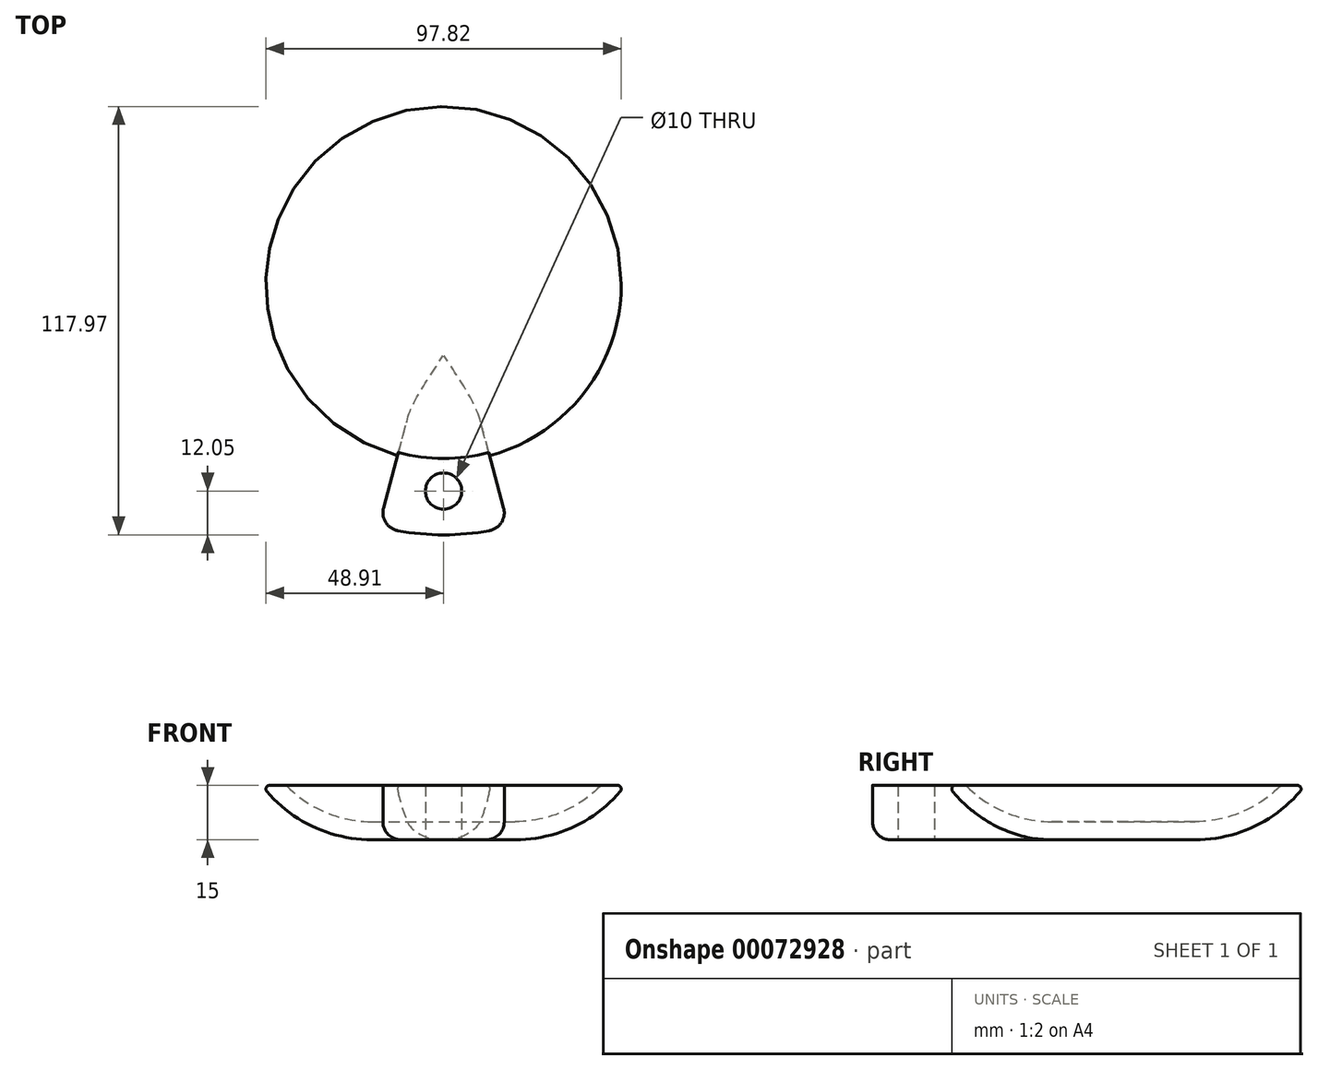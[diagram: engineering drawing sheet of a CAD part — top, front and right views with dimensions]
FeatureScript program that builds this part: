
annotation { "Feature Type Name" : "Feature", "Feature Type Description" : "" }
export const myFeature = defineFeature(function(context is Context, id is Id, definition is map)
    precondition{}
    {
        {
            var Q0;
            Q0=qCreatedBy(makeId("Top.planeOp"),FACE);
            var sketch = newSketch(context, id + "F0", { "sketchPlane" : qUnion([Q0])});
            skCircle(sketch, "E0", {"center": v(0, 0) * mm, "radius": 50 * mm});
            skSolve(sketch);
        }
        {
            var Q0;
            Q0=makeQuery(id+"F0.imprint","IMPRINT",FACE,{"disambiguationData":[TD([[makeQuery(id+"F0.imprint","IMPRINT",EDGE,{"derivedFrom":sQuery(id+"F0.wireOp",EDGE,"E0")}),1.0]])]});
            extrude(context, id + "F1", {"entities" : qUnion([Q0]), "depth" : 15 * mm});
        }
        {
            var Q0;
            Q0=makeQuery(id+"F1.opExtrude","CAP_EDGE",EDGE,{"disambiguationData":[OSD([sQuery(id+"F0.wireOp",EDGE,"E0")])],"isStart":true});
            fillet(context, id + "F2", {"entities" : qUnion([Q0]), "radius" : 38.1 * mm, "tangentPropagation" : true, "allowEdgeOverflow" : false});
        }
        {
            var Q0;
            Q0=makeQuery(id+"F1.opExtrude","CAP_FACE",FACE,{"disambiguationData":[OSD([sQuery(id+"F0.wireOp",EDGE,"E0")])],"isStart":false});
            shell(context, id + "F3", {"entities" : qUnion([Q0]), "thickness" : 5 * mm});
        }
        {
            var Q0;
            {var subQ0=sQuery(id+"F0.wireOp",EDGE,"E0");Q0=makeQuery(id+"F3.opShell","OFFSET_EDGE",EDGE,{"disambiguationData":[OSD([subQ0]),TDD([makeQuery(id+"F2.opFillet","BLEND_EDGE",EDGE,{"blendedFrom":[makeQuery(id+"F1.opExtrude","CAP_EDGE",EDGE,{"disambiguationData":[OSD([subQ0])],"isStart":true}),makeQuery(id+"F1.opExtrude","CAP_FACE",FACE,{"disambiguationData":[OSD([subQ0])],"isStart":false})],"blendedInto":[makeQuery(id+"F1.opExtrude","CAP_FACE",FACE,{"disambiguationData":[OSD([subQ0])],"isStart":false})]})])]});}
            fillet(context, id + "F4", {"entities" : qUnion([Q0]), "radius" : 1 * mm, "allowEdgeOverflow" : false});
        }
        {
            var Q0;
            {var subQ0=sQuery(id+"F0.wireOp",EDGE,"E0");Q0=makeQuery(id+"F2.opFillet","BLEND_EDGE",EDGE,{"blendedFrom":[makeQuery(id+"F1.opExtrude","CAP_EDGE",EDGE,{"disambiguationData":[OSD([subQ0])],"isStart":true}),makeQuery(id+"F1.opExtrude","CAP_FACE",FACE,{"disambiguationData":[OSD([subQ0])],"isStart":false})],"blendedInto":[makeQuery(id+"F1.opExtrude","CAP_FACE",FACE,{"disambiguationData":[OSD([subQ0])],"isStart":false})]});}
            fillet(context, id + "F5", {"entities" : qUnion([Q0]), "radius" : 1 * mm, "allowEdgeOverflow" : false});
        }
        {
            var Q0;
            Q0=qCreatedBy(makeId("Right.planeOp"),FACE);
            var sketch = newSketch(context, id + "F6", { "sketchPlane" : qUnion([Q0])});
            skLineSegment(sketch, "E1", {"start": v(-69.06, 0) * mm, "end": v(-69.06, 15) * mm});
            skLineSegment(sketch, "E2", {"start": v(-69.06, 0) * mm, "end": v(0, 0) * mm});
            skArc(sketch, "E3", {"start": v(-48.02, 15) * mm, "mid": v(-25.15, 3.84) * mm, "end": v(0, 0) * mm});
            skLineSegment(sketch, "E4", {"start": v(-48.02, 15) * mm, "end": v(-69.06, 15) * mm});
            skSolve(sketch);
        }
        {
            var Q0;
            Q0=qCreatedBy(makeId("Right.planeOp"),FACE);
            var sketch = newSketch(context, id + "F7", { "sketchPlane" : qUnion([Q0])});
            skLineSegment(sketch, "E5", {"start": v(0, 44.96) * mm, "end": v(0, 0) * mm, "construction": true});
            skSolve(sketch);
        }
        {
            var Q0;
            Q0=makeQuery(id+"F6.imprint","IMPRINT",FACE,{"disambiguationData":[TD([[makeQuery(id+"F6.imprint","IMPRINT",EDGE,{"derivedFrom":sQuery(id+"F6.wireOp",EDGE,"E1")}),-1.0]])]});
            var Q1;
            Q1=sQuery(id+"F7.wireOp",EDGE,"E5");
            revolve(context, id + "F8", {"operationType" : NewBodyOperationType.ADD, "entities" : qUnion([Q0]), "axis" : qUnion([Q1]), "revolveType" : RevolveType.SYMMETRIC, "angle" : 30 * degree});
        }
        {
            var Q0;
            Q0=makeQuery(id+"F8.opRevolve","SWEPT_EDGE",EDGE,{"disambiguationData":[OSD([sQuery(id+"F6.wireOp",EDGE,"E1"),sQuery(id+"F6.wireOp",EDGE,"E2")])]});
            var Q1;
            Q1=makeQuery(id+"F8.opRevolve","CAP_EDGE",EDGE,{"disambiguationData":[OSD([sQuery(id+"F6.wireOp",EDGE,"E2")])],"isStart":true});
            var Q2;
            Q2=makeQuery(id+"F8.opRevolve","CAP_EDGE",EDGE,{"disambiguationData":[OSD([sQuery(id+"F6.wireOp",EDGE,"E2")])],"isStart":false});
            var Q3;
            Q3=makeQuery(id+"F8.opRevolve","CAP_EDGE",EDGE,{"disambiguationData":[OSD([sQuery(id+"F6.wireOp",EDGE,"E1")])],"isStart":true});
            var Q4;
            Q4=makeQuery(id+"F8.opRevolve","CAP_EDGE",EDGE,{"disambiguationData":[OSD([sQuery(id+"F6.wireOp",EDGE,"E1")])],"isStart":false});
            fillet(context, id + "F9", {"entities" : qUnion([Q0, Q1, Q2, Q3, Q4]), "radius" : 5 * mm, "tangentPropagation" : true, "allowEdgeOverflow" : false});
        }
        {
            var Q0;
            Q0=qCreatedBy(makeId("Top.planeOp"),FACE);
            var sketch = newSketch(context, id + "F10", { "sketchPlane" : qUnion([Q0])});
            skCircle(sketch, "E6", {"center": v(0, -57) * mm, "radius": 5 * mm});
            skSolve(sketch);
        }
        {
            var Q0;
            Q0 = qSketchRegion(id + "F10", true);
            extrude(context, id + "F11", {"entities" : qUnion([Q0]), "operationType" : NewBodyOperationType.REMOVE, "depth" : 20 * mm});
        }
    });
